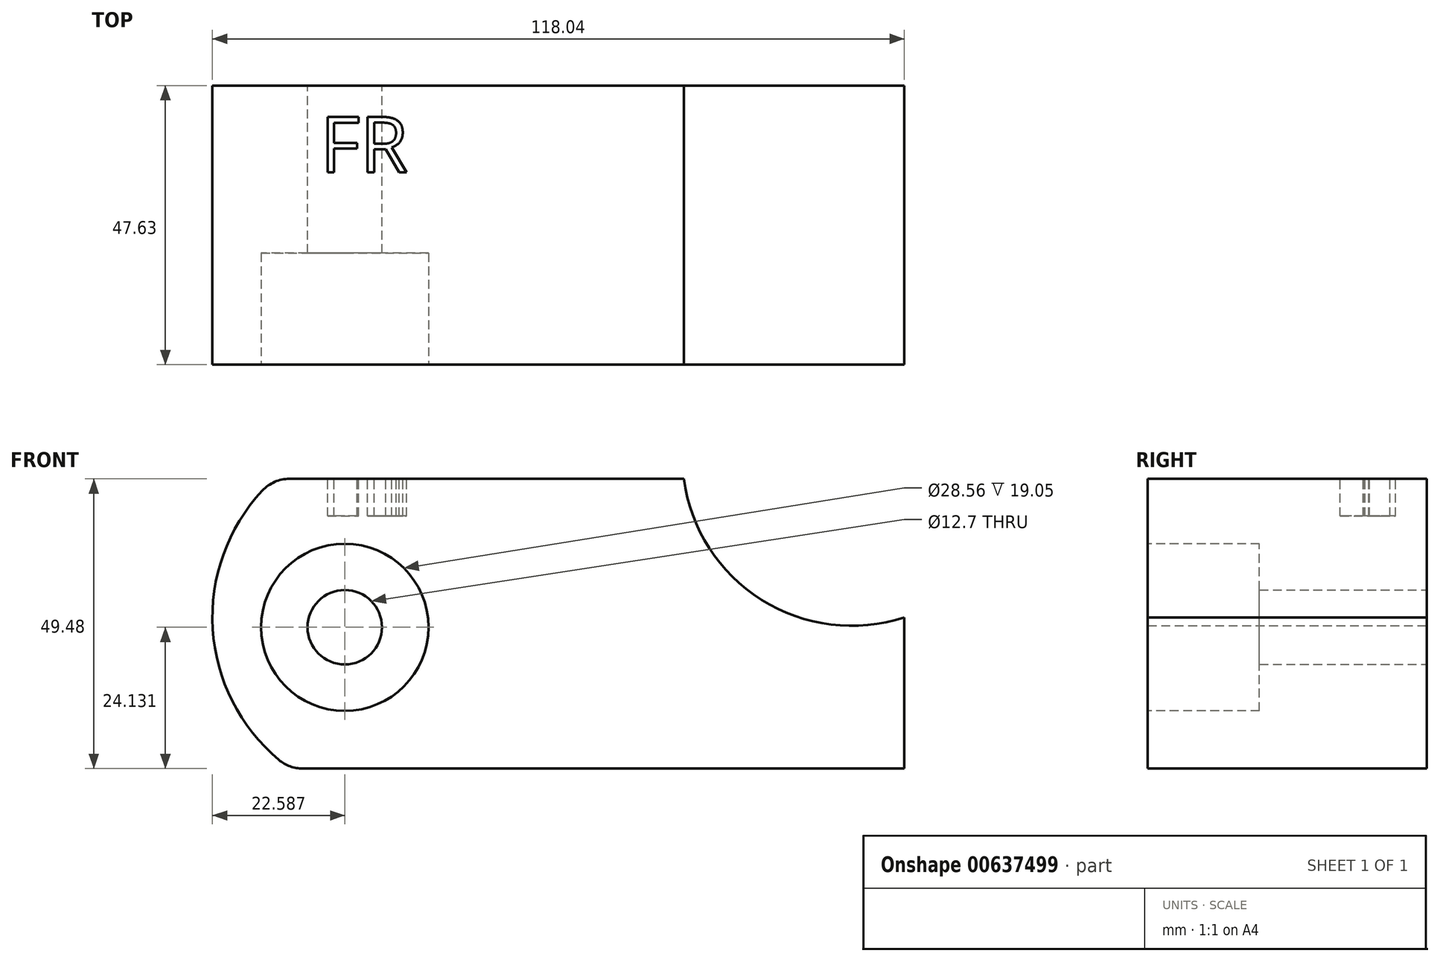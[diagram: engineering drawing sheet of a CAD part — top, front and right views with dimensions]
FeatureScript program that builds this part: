
annotation { "Feature Type Name" : "Feature", "Feature Type Description" : "" }
export const myFeature = defineFeature(function(context is Context, id is Id, definition is map)
    precondition{}
    {
        {
            var Q0;
            Q0=qCreatedBy(makeId("Front.planeOp"),FACE);
            var sketch = newSketch(context, id + "F0", { "sketchPlane" : qUnion([Q0])});
            skArc(sketch, "E0", {"start": v(-48.5, 28.25) * mm, "mid": v(-59.04, 2.87) * mm, "end": v(-45.82, -21.23) * mm});
            skLineSegment(sketch, "E1", {"start": v(-45.82, -21.23) * mm, "end": v(58.96, -21.23) * mm});
            skLineSegment(sketch, "E2", {"start": v(58.96, -21.23) * mm, "end": v(58.96, 4.58) * mm});
            skLineSegment(sketch, "E3", {"start": v(-48.5, 28.25) * mm, "end": v(21.35, 28.25) * mm});
            skArc(sketch, "E4", {"start": v(21.35, 28.25) * mm, "mid": v(34.6, 7.59) * mm, "end": v(58.96, 4.58) * mm});
            skSolve(sketch);
        }
        {
            var Q0;
            Q0=makeQuery(id+"F0.imprint","IMPRINT",FACE,{"disambiguationData":[TD([[makeQuery(id+"F0.imprint","IMPRINT",EDGE,{"derivedFrom":sQuery(id+"F0.wireOp",EDGE,"E0")}),1.0]])]});
            extrude(context, id + "F1", {"entities" : qUnion([Q0]), "depth" : 47.62 * mm, "offsetDistance" : 25.4 * mm});
        }
        {
            var Q0;
            Q0=makeQuery(id+"F1.opExtrude","SWEPT_EDGE",EDGE,{"disambiguationData":[OSD([sQuery(id+"F0.wireOp",EDGE,"E0"),sQuery(id+"F0.wireOp",EDGE,"E3")])]});
            var Q1;
            Q1=makeQuery(id+"F1.opExtrude","SWEPT_EDGE",EDGE,{"disambiguationData":[OSD([sQuery(id+"F0.wireOp",EDGE,"E0"),sQuery(id+"F0.wireOp",EDGE,"E1")])]});
            fillet(context, id + "F2", {"entities" : qUnion([Q0, Q1]), "radius" : 6.35 * mm, "tangentPropagation" : true, "allowEdgeOverflow" : false});
        }
        {
            var Q0;
            Q0=makeQuery(id+"F1.opExtrude","CAP_FACE",FACE,{"disambiguationData":[OSD([sQuery(id+"F0.wireOp",EDGE,"E0"),sQuery(id+"F0.wireOp",EDGE,"E1"),sQuery(id+"F0.wireOp",EDGE,"E2"),sQuery(id+"F0.wireOp",EDGE,"E3"),sQuery(id+"F0.wireOp",EDGE,"E4")])],"isStart":false});
            var sketch = newSketch(context, id + "F3", { "sketchPlane" : qUnion([Q0])});
            skCircle(sketch, "E5", {"center": v(-36.5, 2.9) * mm, "radius": 14.28 * mm});
            skSolve(sketch);
        }
        {
            var Q0;
            Q0=makeQuery(id+"F3.imprint","IMPRINT",FACE,{"disambiguationData":[TD([[makeQuery(id+"F3.imprint","IMPRINT",EDGE,{"derivedFrom":sQuery(id+"F3.wireOp",EDGE,"E5")}),1.0]])]});
            extrude(context, id + "F4", {"entities" : qUnion([Q0]), "operationType" : NewBodyOperationType.REMOVE, "endBound" : BoundingType.THROUGH_ALL, "oppositeDirection" : true, "depth" : 25.4 * mm, "offsetDistance" : 25.4 * mm});
        }
        {
            var Q0;
            Q0=makeQuery(id+"F1.opExtrude","SWEPT_FACE",FACE,{"disambiguationData":[OSD([sQuery(id+"F0.wireOp",EDGE,"E3")])]});
            var sketch = newSketch(context, id + "F5", { "sketchPlane" : qUnion([Q0])});
            skText(sketch, "E6", { "text": "FR", "fontName": "OpenSans-Regular.ttf"});
            const initialGuessF5  = {"E6": [-0.04074, -0.0148, 1, 0, 0.00954]};
            skSetInitialGuess(sketch, initialGuessF5);
            skSolve(sketch);
        }
        {
            var Q0;
            Q0 = qSketchRegion(id + "F5", true);
            extrude(context, id + "F6", {"entities" : qUnion([Q0]), "operationType" : NewBodyOperationType.REMOVE, "oppositeDirection" : true, "depth" : 6.35 * mm, "offsetDistance" : 25.4 * mm});
        }
        {
            var Q0;
            Q0=qCreatedBy(makeId("Front.planeOp"),FACE);
            var sketch = newSketch(context, id + "F7", { "sketchPlane" : qUnion([Q0])});
            skCircle(sketch, "E7", {"center": v(-36.5, 2.9) * mm, "radius": 14.28 * mm});
            skCircle(sketch, "E8", {"center": v(-36.5, 2.9) * mm, "radius": 6.35 * mm});
            skSolve(sketch);
        }
        {
            var Q0;
            Q0 = qSketchRegion(id + "F7", true);
            extrude(context, id + "F8", {"entities" : qUnion([Q0]), "operationType" : NewBodyOperationType.ADD, "depth" : 28.57 * mm, "offsetDistance" : 25.4 * mm});
        }
    });
